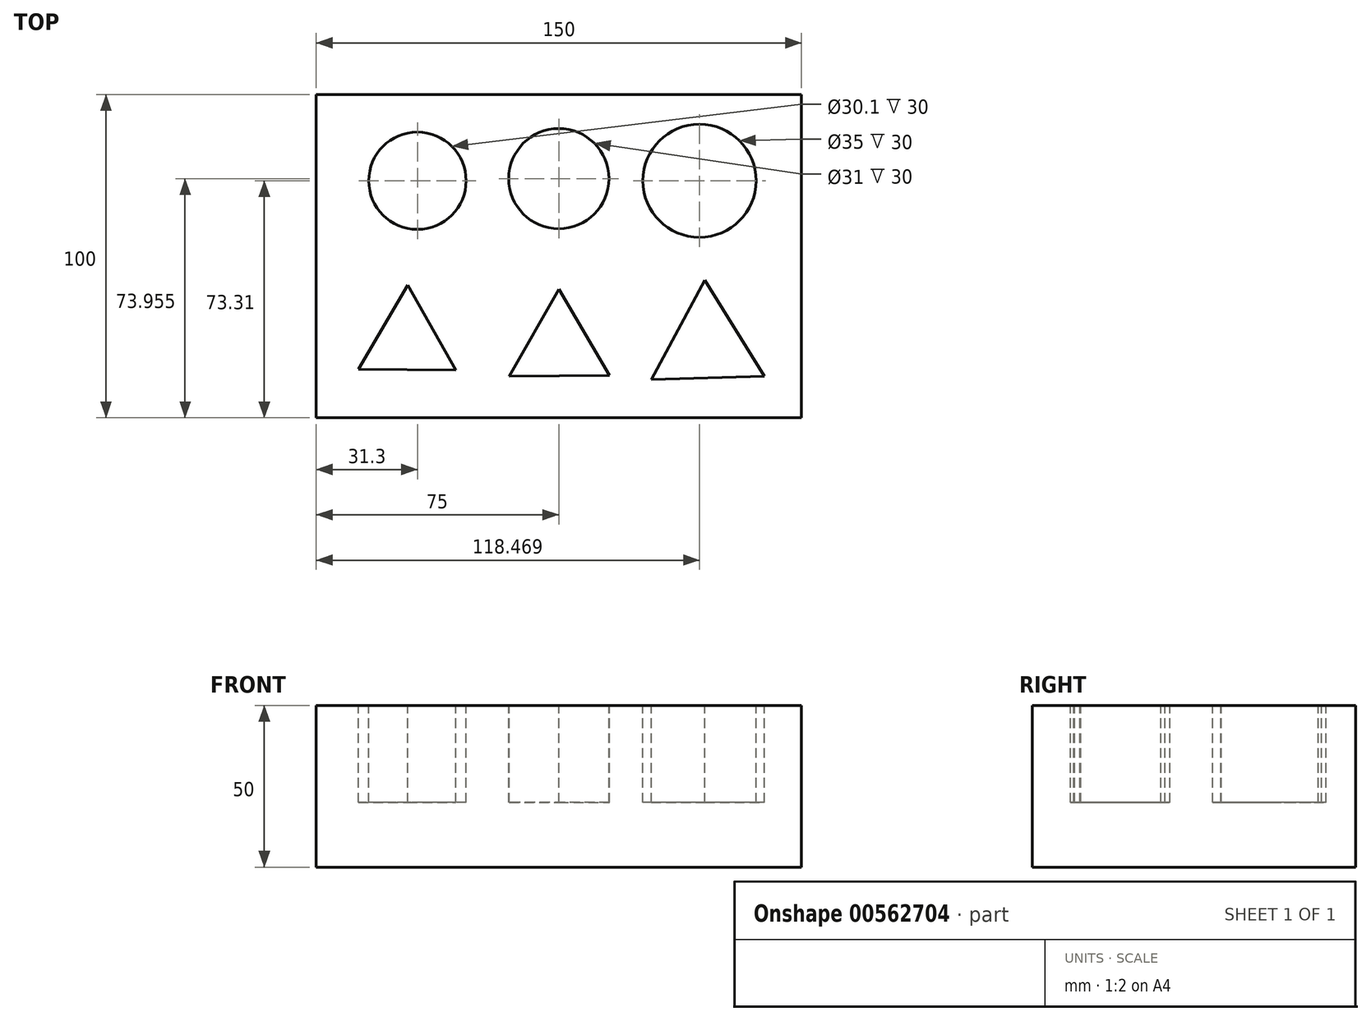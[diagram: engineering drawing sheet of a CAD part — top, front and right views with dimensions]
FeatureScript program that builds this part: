
annotation { "Feature Type Name" : "Feature", "Feature Type Description" : "" }
export const myFeature = defineFeature(function(context is Context, id is Id, definition is map)
    precondition{}
    {
        {
            var Q0;
            Q0=qCreatedBy(makeId("Top.planeOp"),FACE);
            var sketch = newSketch(context, id + "F0", { "sketchPlane" : qUnion([Q0])});
            skLineSegment(sketch, "E0.bottom", {"start": v(75, -50) * mm, "end": v(-75, -50) * mm});
            skLineSegment(sketch, "E0.top", {"start": v(75, 50) * mm, "end": v(-75, 50) * mm});
            skLineSegment(sketch, "E0.left", {"start": v(75, -50) * mm, "end": v(75, 50) * mm});
            skLineSegment(sketch, "E0.right", {"start": v(-75, -50) * mm, "end": v(-75, 50) * mm});
            skPoint(sketch, "E0.middle", {"position": v(0, 0) * mm});
            skSolve(sketch);
        }
        {
            var Q0;
            Q0=makeQuery(id+"F0.imprint","IMPRINT",FACE,{"disambiguationData":[TD([[makeQuery(id+"F0.imprint","IMPRINT",EDGE,{"derivedFrom":sQuery(id+"F0.wireOp",EDGE,"E0.bottom")}),-1.0]])]});
            extrude(context, id + "F1", {"entities" : qUnion([Q0]), "depth" : 50 * mm, "offsetDistance" : 25.4 * mm});
        }
        {
            var Q0;
            Q0=makeQuery(id+"F1.opExtrude","CAP_FACE",FACE,{"disambiguationData":[OSD([sQuery(id+"F0.wireOp",EDGE,"E0.bottom"),sQuery(id+"F0.wireOp",EDGE,"E0.top"),sQuery(id+"F0.wireOp",EDGE,"E0.left"),sQuery(id+"F0.wireOp",EDGE,"E0.right")])],"isStart":false});
            var sketch = newSketch(context, id + "F2", { "sketchPlane" : qUnion([Q0])});
            skCircle(sketch, "E1", {"center": v(-43.7, 23.3) * mm, "radius": 15.05 * mm});
            skCircle(sketch, "E2", {"center": v(0, 23.96) * mm, "radius": 15.5 * mm});
            skCircle(sketch, "E3", {"center": v(43.47, 23.3) * mm, "radius": 17.5 * mm});
            skCircle(sketch, "E4.cCircle", {"center": v(-46.84, -26.4) * mm, "radius": 17.38 * mm, "construction": true});
            skLineSegment(sketch, "E4.0", {"start": v(-31.85, -35.2) * mm, "end": v(-61.94, -35) * mm});
            skLineSegment(sketch, "E4.1", {"start": v(-61.94, -35) * mm, "end": v(-46.72, -9.02) * mm});
            skLineSegment(sketch, "E4.2", {"start": v(-46.72, -9.02) * mm, "end": v(-31.85, -35.2) * mm});
            skCircle(sketch, "E5.cCircle", {"center": v(0.14, -28.08) * mm, "radius": 17.9 * mm, "construction": true});
            skLineSegment(sketch, "E5.0", {"start": v(15.7, -36.91) * mm, "end": v(-15.3, -37.15) * mm});
            skLineSegment(sketch, "E5.1", {"start": v(-15.3, -37.15) * mm, "end": v(0, -10.18) * mm});
            skLineSegment(sketch, "E5.2", {"start": v(0, -10.18) * mm, "end": v(15.7, -36.91) * mm});
            skCircle(sketch, "E6.cCircle", {"center": v(45.78, -27.6) * mm, "radius": 20.2 * mm, "construction": true});
            skLineSegment(sketch, "E6.0", {"start": v(63.58, -37.18) * mm, "end": v(28.6, -38.23) * mm});
            skLineSegment(sketch, "E6.1", {"start": v(28.6, -38.23) * mm, "end": v(45.17, -7.4) * mm});
            skLineSegment(sketch, "E6.2", {"start": v(45.17, -7.4) * mm, "end": v(63.58, -37.18) * mm});
            skSolve(sketch);
        }
        {
            var Q0;
            Q0=makeQuery(id+"F2.imprint","IMPRINT",FACE,{"disambiguationData":[TD([[makeQuery(id+"F2.imprint","IMPRINT",EDGE,{"derivedFrom":sQuery(id+"F2.wireOp",EDGE,"E1")}),1.0]])]});
            var Q1;
            Q1=makeQuery(id+"F2.imprint","IMPRINT",FACE,{"disambiguationData":[TD([[makeQuery(id+"F2.imprint","IMPRINT",EDGE,{"derivedFrom":sQuery(id+"F2.wireOp",EDGE,"E2")}),1.0]])]});
            var Q2;
            Q2=makeQuery(id+"F2.imprint","IMPRINT",FACE,{"disambiguationData":[TD([[makeQuery(id+"F2.imprint","IMPRINT",EDGE,{"derivedFrom":sQuery(id+"F2.wireOp",EDGE,"E3")}),1.0]])]});
            var Q3;
            Q3=makeQuery(id+"F2.imprint","IMPRINT",FACE,{"disambiguationData":[TD([[makeQuery(id+"F2.imprint","IMPRINT",EDGE,{"derivedFrom":sQuery(id+"F2.wireOp",EDGE,"E4.0")}),-1.0]])]});
            var Q4;
            Q4=makeQuery(id+"F2.imprint","IMPRINT",FACE,{"disambiguationData":[TD([[makeQuery(id+"F2.imprint","IMPRINT",EDGE,{"derivedFrom":sQuery(id+"F2.wireOp",EDGE,"E5.0")}),-1.0]])]});
            var Q5;
            Q5=makeQuery(id+"F2.imprint","IMPRINT",FACE,{"disambiguationData":[TD([[makeQuery(id+"F2.imprint","IMPRINT",EDGE,{"derivedFrom":sQuery(id+"F2.wireOp",EDGE,"E6.0")}),-1.0]])]});
            extrude(context, id + "F3", {"entities" : qUnion([Q0, Q1, Q2, Q3, Q4, Q5]), "operationType" : NewBodyOperationType.REMOVE, "oppositeDirection" : true, "depth" : 30 * mm, "offsetDistance" : 25.4 * mm});
        }
    });
